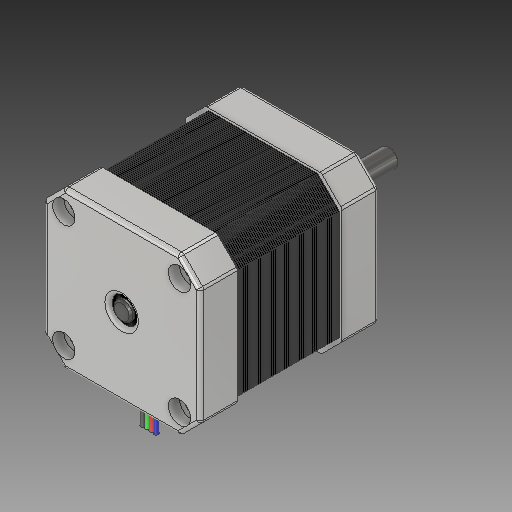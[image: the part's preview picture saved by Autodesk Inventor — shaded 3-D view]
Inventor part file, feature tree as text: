
AUTODESK INVENTOR PART (.ipt)
format: ipt  version: 2017 (Build 210142000, 142)  size: 1,358,848 bytes
history: native  units: mm
features: sketch x5, other x3
ambient origin geometry x8: Origin, YZ Plane, XZ Plane, XY Plane, X Axis, Y Axis, Z Axis, Center Point
bodies: Solid1 (feature_tree)
feature tree (8):
  other  "Nema17_CPY.ipt"
  other  "Solid1::Nema17_CPY.ipt"
  other  "TaggingFeature1"
  sketch  "Sketch1"  dims[d0=10.0mm]
  sketch  "Sketch4"
  sketch  "Sketch5"
  sketch  "Sketch6"
  sketch  "Sketch11"
